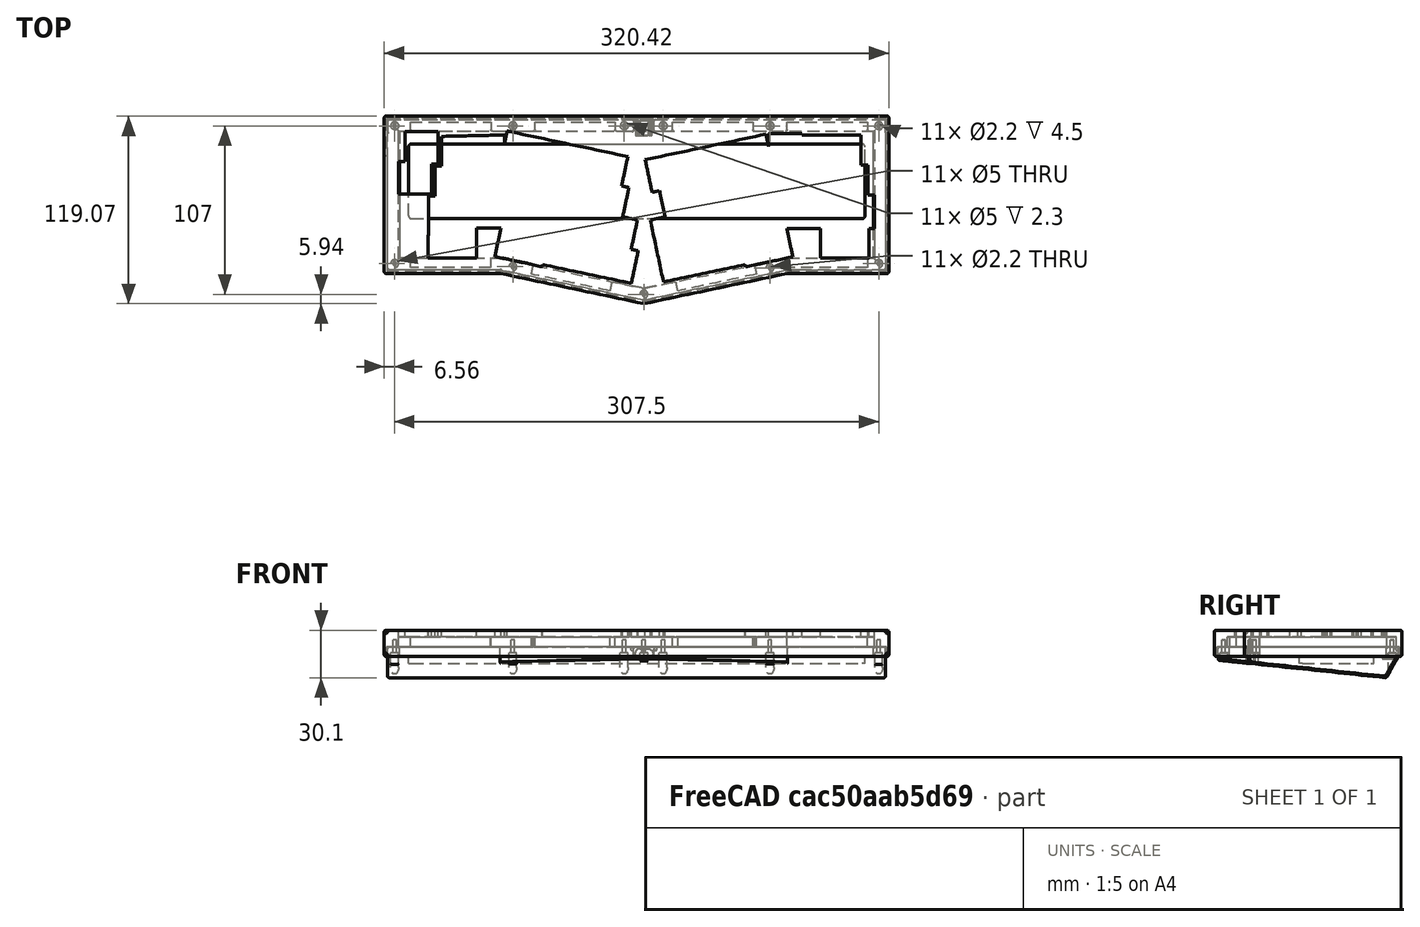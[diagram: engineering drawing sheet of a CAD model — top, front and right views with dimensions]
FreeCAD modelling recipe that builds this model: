
FCSTD DOCUMENT  (FreeCAD 0.19R24291 (Git))
Label: vision-case
License: All rights reserved
LicenseURL: http://en.wikipedia.org/wiki/All_rights_reserved
objects: Part::Cylinder×48, Part::Feature×12, Part::MultiFuse×10, Part::Extrusion×7, Part::Cut×7, Part::Fillet×7, Part::Box×2, Part::FeaturePython×2, Part::Common×1, Part::MultiCommon×1
note: 97 computed .brp shape members not serialized (recipe doc carries the construction recipe); baked Part::Feature solids carry a one-line shape summary decoded from their .brp

FEATURE [Part::Feature] path1505_004
  Placement = pos=(0,-0.8,-22.5) rot=(-1,0,0;0.10472rad)
  shape: bbox 316.2 x 114.2 x 12.01 mm, 0 faces, 0 solids (baked)
FEATURE [Part::Extrusion] Extrude
  Base = -> path1505_004
  Dir = (0,0,1)
  DirMode = 0
  FaceMakerClass = Part::FaceMakerBullseye
  LengthFwd = 100
  LengthRev = 0
  Solid = true
  Symmetric = false
FEATURE [Part::Feature] path1505_3
  shape: bbox 316.2 x 114.9 x 2e-07 mm, 0 faces, 0 solids (baked)
FEATURE [Part::Extrusion] Extrude001
  Base = -> path1505_3
  Dir = (0,0,-1)
  DirMode = 0
  FaceMakerClass = Part::FaceMakerBullseye
  LengthFwd = 100
  LengthRev = 0
  Solid = true
  Symmetric = false
FEATURE [Part::Common] Common
  Base = -> Extrude
  Tool = -> Extrude001
FEATURE [Part::Box] Box  label="立方体"
  AttacherType = Attacher::AttachEngine3D
  Height = 30
  Length = 400
  Placement = pos=(0,-88.5,-20) rot=(-1,0,0;0.523599rad)
  Width = 30
FEATURE [Part::Cut] Cut
  Base = -> Common
  Tool = -> Box
FEATURE [Part::Fillet] Fillet001  label="bottom-base"
  Base = -> Cut
  Edges = 15 edges r=1: [Edge1,Edge2,Edge4,Edge5,Edge6,Edge7,Edge8,Edge9,Edge10,Edge11,Edge18,Edge19,Edge20,Edge21,Edge22]
FEATURE [Part::Feature] path1529_1
  shape: bbox 320.4 x 119.1 x 2e-07 mm, 0 faces, 0 solids (baked)
FEATURE [Part::Feature] path1529_1001
  shape: bbox 317.2 x 115.9 x 2e-07 mm, 0 faces, 0 solids (baked)
FEATURE [Part::MultiFuse] Fusion
  Shapes = -> [path1529_1001,path1529_1]
FEATURE [Part::Feature] path1795_9
  shape: bbox 302.2 x 107.3 x 2e-07 mm, 0 faces, 0 solids (baked)
FEATURE [Part::Feature] path1795_9001
  shape: bbox 320.4 x 119.1 x 2e-07 mm, 0 faces, 0 solids (baked)
FEATURE [Part::MultiFuse] Fusion001
  Placement = pos=(0,0,5.8) rot=(0,0,1;0rad)
  Shapes = -> [path1795_9001,path1795_9]
FEATURE [Part::Extrusion] Extrude003  label="under-middle-base"
  Base = -> Fusion
  Dir = (0,0,1)
  DirMode = 0
  FaceMakerClass = Part::FaceMakerBullseye
  LengthFwd = 5.8
  LengthRev = 0
  Solid = true
  Symmetric = false
FEATURE [Part::Extrusion] Extrude004  label="middle-base"
  Base = -> Fusion001
  Dir = (0,0,1)
  DirMode = 0
  FaceMakerClass = Part::FaceMakerBullseye
  LengthFwd = 6.6
  LengthRev = 0
  Solid = true
  Symmetric = false
FEATURE [Part::Fillet] Fillet002  label="under-middle-base001"
  Base = -> Extrude003
  Edges = 14 edges r=1: [Edge1,Edge2,Edge3,Edge5,Edge6,Edge8,Edge9,Edge11,Edge12,Edge14,Edge15,Edge17,Edge18,Edge20]
FEATURE [Part::Fillet] Fillet003  label="middle-base001"
  Base = -> Extrude004
  Edges = 25 edges r=1: [Edge1,Edge2,Edge5,Edge8,Edge11,Edge14,Edge17,Edge22,Edge23,Edge32,Edge35,Edge44,Edge53,Edge62,Edge68,Edge77,Edge83,Edge92,Edge98,Edge107,Edge116,Edge125,Edge128,Edge131,Edge140]
FEATURE [Part::Cylinder] Cylinder  label="円柱"
  Angle = 360
  AttacherType = Attacher::AttachEngine3D
  Height = 30
  Placement = pos=(51.7,-81,-27.7) rot=(0,0,1;0rad)
  Radius = 2.5
FEATURE [Part::Cylinder] Cylinder001  label="円柱001"
  Angle = 360
  AttacherType = Attacher::AttachEngine3D
  Height = 30
  Placement = pos=(359.2,-81,-27.7) rot=(0,0,1;0rad)
  Radius = 2.5
FEATURE [Part::Cylinder] Cylinder002  label="円柱002"
  Angle = 360
  AttacherType = Attacher::AttachEngine3D
  Height = 30
  Placement = pos=(126.8,-81,-27.7) rot=(0,0,1;0rad)
  Radius = 2.5
FEATURE [Part::Cylinder] Cylinder003  label="円柱003"
  Angle = 360
  AttacherType = Attacher::AttachEngine3D
  Height = 30
  Placement = pos=(197.5,-81,-27.7) rot=(0,0,1;0rad)
  Radius = 2.5
FEATURE [Part::Cylinder] Cylinder004  label="円柱004"
  Angle = 360
  AttacherType = Attacher::AttachEngine3D
  Height = 30
  Placement = pos=(290.1,-81,-27.7) rot=(0,0,1;0rad)
  Radius = 2.5
FEATURE [Part::Cylinder] Cylinder005  label="円柱005"
  Angle = 360
  AttacherType = Attacher::AttachEngine3D
  Height = 30
  Placement = pos=(222.2,-81,-27.7) rot=(0,0,1;0rad)
  Radius = 2.5
FEATURE [Part::Cylinder] Cylinder006  label="円柱006"
  Angle = 360
  AttacherType = Attacher::AttachEngine3D
  Height = 30
  Placement = pos=(51.7,-168.5,-27.7) rot=(0,0,1;0rad)
  Radius = 2.5
FEATURE [Part::Cylinder] Cylinder007  label="円柱007"
  Angle = 360
  AttacherType = Attacher::AttachEngine3D
  Height = 30
  Placement = pos=(359.2,-168.5,-27.7) rot=(0,0,1;0rad)
  Radius = 2.5
FEATURE [Part::Cylinder] Cylinder008  label="円柱008"
  Angle = 360
  AttacherType = Attacher::AttachEngine3D
  Height = 30
  Placement = pos=(126.8,-170.5,-27.7) rot=(0,0,1;0rad)
  Radius = 2.5
FEATURE [Part::Cylinder] Cylinder009  label="円柱009"
  Angle = 360
  AttacherType = Attacher::AttachEngine3D
  Height = 30
  Placement = pos=(290.1,-171.2,-27.7) rot=(0,0,1;0rad)
  Radius = 2.5
FEATURE [Part::Cylinder] Cylinder010  label="円柱010"
  Angle = 360
  AttacherType = Attacher::AttachEngine3D
  Height = 30
  Placement = pos=(210,-188,-27.7) rot=(0,0,1;0rad)
  Radius = 2.5
FEATURE [Part::MultiFuse] Fusion003
  Shapes = -> [Cylinder010,Cylinder009,Cylinder008,Cylinder007,Cylinder006,Cylinder005,Cylinder004,Cylinder003,Cylinder002,Cylinder001,Cylinder]
FEATURE [Part::Cylinder] Cylinder011  label="円柱011"
  Angle = 360
  AttacherType = Attacher::AttachEngine3D
  Height = 38
  Placement = pos=(126.8,-170.5,-27.7) rot=(0,0,1;0rad)
  Radius = 1.1
FEATURE [Part::Cylinder] Cylinder012  label="円柱012"
  Angle = 360
  AttacherType = Attacher::AttachEngine3D
  Height = 38
  Placement = pos=(290.1,-171.2,-27.7) rot=(0,0,1;0rad)
  Radius = 1.1
FEATURE [Part::Cylinder] Cylinder013  label="円柱013"
  Angle = 360
  AttacherType = Attacher::AttachEngine3D
  Height = 38
  Placement = pos=(126.8,-81,-27.7) rot=(0,0,1;0rad)
  Radius = 1.1
FEATURE [Part::Cylinder] Cylinder014  label="円柱014"
  Angle = 360
  AttacherType = Attacher::AttachEngine3D
  Height = 38
  Placement = pos=(210,-188,-27.7) rot=(0,0,1;0rad)
  Radius = 1.1
FEATURE [Part::Cylinder] Cylinder015  label="円柱015"
  Angle = 360
  AttacherType = Attacher::AttachEngine3D
  Height = 38
  Placement = pos=(359.2,-81,-27.7) rot=(0,0,1;0rad)
  Radius = 1.1
FEATURE [Part::Cylinder] Cylinder016  label="円柱016"
  Angle = 360
  AttacherType = Attacher::AttachEngine3D
  Height = 38
  Placement = pos=(197.5,-81,-27.7) rot=(0,0,1;0rad)
  Radius = 1.1
FEATURE [Part::Cylinder] Cylinder017  label="円柱017"
  Angle = 360
  AttacherType = Attacher::AttachEngine3D
  Height = 38
  Placement = pos=(290.1,-81,-27.7) rot=(0,0,1;0rad)
  Radius = 1.1
FEATURE [Part::Cylinder] Cylinder018  label="円柱018"
  Angle = 360
  AttacherType = Attacher::AttachEngine3D
  Height = 38
  Placement = pos=(51.7,-81,-27.7) rot=(0,0,1;0rad)
  Radius = 1.1
FEATURE [Part::Cylinder] Cylinder019  label="円柱019"
  Angle = 360
  AttacherType = Attacher::AttachEngine3D
  Height = 38
  Placement = pos=(222.2,-81,-27.7) rot=(0,0,1;0rad)
  Radius = 1.1
FEATURE [Part::Cylinder] Cylinder020  label="円柱020"
  Angle = 360
  AttacherType = Attacher::AttachEngine3D
  Height = 38
  Placement = pos=(359.2,-168.5,-27.7) rot=(0,0,1;0rad)
  Radius = 1.1
FEATURE [Part::Cylinder] Cylinder021  label="円柱021"
  Angle = 360
  AttacherType = Attacher::AttachEngine3D
  Height = 38
  Placement = pos=(51.7,-168.5,-27.7) rot=(0,0,1;0rad)
  Radius = 1.1
FEATURE [Part::MultiFuse] Fusion004
  Shapes = -> [Cylinder014,Cylinder012,Cylinder011,Cylinder020,Cylinder021,Cylinder019,Cylinder017,Cylinder016,Cylinder013,Cylinder015,Cylinder018]
FEATURE [Part::Cylinder] Cylinder022  label="円柱022"
  Angle = 360
  AttacherType = Attacher::AttachEngine3D
  Height = 30
  Placement = pos=(126.8,-170.5,-27.7) rot=(0,0,1;0rad)
  Radius = 2.5
FEATURE [Part::Cylinder] Cylinder023  label="円柱023"
  Angle = 360
  AttacherType = Attacher::AttachEngine3D
  Height = 30
  Placement = pos=(290.1,-171.2,-27.7) rot=(0,0,1;0rad)
  Radius = 2.5
FEATURE [Part::Cylinder] Cylinder024  label="円柱024"
  Angle = 360
  AttacherType = Attacher::AttachEngine3D
  Height = 30
  Placement = pos=(126.8,-81,-27.7) rot=(0,0,1;0rad)
  Radius = 2.5
FEATURE [Part::Cylinder] Cylinder025  label="円柱025"
  Angle = 360
  AttacherType = Attacher::AttachEngine3D
  Height = 30
  Placement = pos=(210,-188,-27.7) rot=(0,0,1;0rad)
  Radius = 2.5
FEATURE [Part::Cylinder] Cylinder026  label="円柱026"
  Angle = 360
  AttacherType = Attacher::AttachEngine3D
  Height = 30
  Placement = pos=(359.2,-81,-27.7) rot=(0,0,1;0rad)
  Radius = 2.5
FEATURE [Part::Cylinder] Cylinder027  label="円柱027"
  Angle = 360
  AttacherType = Attacher::AttachEngine3D
  Height = 30
  Placement = pos=(197.5,-81,-27.7) rot=(0,0,1;0rad)
  Radius = 2.5
FEATURE [Part::Cylinder] Cylinder028  label="円柱028"
  Angle = 360
  AttacherType = Attacher::AttachEngine3D
  Height = 30
  Placement = pos=(290.1,-81,-27.7) rot=(0,0,1;0rad)
  Radius = 2.5
FEATURE [Part::Cylinder] Cylinder029  label="円柱029"
  Angle = 360
  AttacherType = Attacher::AttachEngine3D
  Height = 30
  Placement = pos=(51.7,-81,-27.7) rot=(0,0,1;0rad)
  Radius = 2.5
FEATURE [Part::Cylinder] Cylinder030  label="円柱030"
  Angle = 360
  AttacherType = Attacher::AttachEngine3D
  Height = 30
  Placement = pos=(222.2,-81,-27.7) rot=(0,0,1;0rad)
  Radius = 2.5
FEATURE [Part::Cylinder] Cylinder031  label="円柱031"
  Angle = 360
  AttacherType = Attacher::AttachEngine3D
  Height = 30
  Placement = pos=(359.2,-168.5,-27.7) rot=(0,0,1;0rad)
  Radius = 2.5
FEATURE [Part::Cylinder] Cylinder032  label="円柱032"
  Angle = 360
  AttacherType = Attacher::AttachEngine3D
  Height = 30
  Placement = pos=(51.7,-168.5,-27.7) rot=(0,0,1;0rad)
  Radius = 2.5
FEATURE [Part::MultiFuse] Fusion005
  Shapes = -> [Cylinder025,Cylinder023,Cylinder022,Cylinder031,Cylinder032,Cylinder030,Cylinder028,Cylinder027,Cylinder024,Cylinder026,Cylinder029]
FEATURE [Part::Cylinder] Cylinder033  label="円柱033"
  Angle = 360
  AttacherType = Attacher::AttachEngine3D
  Height = 38
  Placement = pos=(126.8,-81,-27.7) rot=(0,0,1;0rad)
  Radius = 1.1
FEATURE [Part::Cylinder] Cylinder034  label="円柱034"
  Angle = 360
  AttacherType = Attacher::AttachEngine3D
  Height = 38
  Placement = pos=(51.7,-81,-27.7) rot=(0,0,1;0rad)
  Radius = 1.1
FEATURE [Part::Cylinder] Cylinder035  label="円柱035"
  Angle = 360
  AttacherType = Attacher::AttachEngine3D
  Height = 38
  Placement = pos=(197.5,-81,-27.7) rot=(0,0,1;0rad)
  Radius = 1.1
FEATURE [Part::Cylinder] Cylinder036  label="円柱036"
  Angle = 360
  AttacherType = Attacher::AttachEngine3D
  Height = 38
  Placement = pos=(222.2,-81,-27.7) rot=(0,0,1;0rad)
  Radius = 1.1
FEATURE [Part::Cylinder] Cylinder037  label="円柱037"
  Angle = 360
  AttacherType = Attacher::AttachEngine3D
  Height = 38
  Placement = pos=(359.2,-168.5,-27.7) rot=(0,0,1;0rad)
  Radius = 1.1
FEATURE [Part::Cylinder] Cylinder038  label="円柱038"
  Angle = 360
  AttacherType = Attacher::AttachEngine3D
  Height = 38
  Placement = pos=(359.2,-81,-27.7) rot=(0,0,1;0rad)
  Radius = 1.1
FEATURE [Part::Cylinder] Cylinder039  label="円柱039"
  Angle = 360
  AttacherType = Attacher::AttachEngine3D
  Height = 38
  Placement = pos=(126.8,-170.5,-27.7) rot=(0,0,1;0rad)
  Radius = 1.1
FEATURE [Part::Cylinder] Cylinder040  label="円柱040"
  Angle = 360
  AttacherType = Attacher::AttachEngine3D
  Height = 38
  Placement = pos=(290.1,-171.2,-27.7) rot=(0,0,1;0rad)
  Radius = 1.1
FEATURE [Part::Cylinder] Cylinder041  label="円柱041"
  Angle = 360
  AttacherType = Attacher::AttachEngine3D
  Height = 38
  Placement = pos=(210,-188,-27.7) rot=(0,0,1;0rad)
  Radius = 1.1
FEATURE [Part::Cylinder] Cylinder042  label="円柱042"
  Angle = 360
  AttacherType = Attacher::AttachEngine3D
  Height = 38
  Placement = pos=(290.1,-81,-27.7) rot=(0,0,1;0rad)
  Radius = 1.1
FEATURE [Part::Cylinder] Cylinder043  label="円柱043"
  Angle = 360
  AttacherType = Attacher::AttachEngine3D
  Height = 38
  Placement = pos=(51.7,-168.5,-27.7) rot=(0,0,1;0rad)
  Radius = 1.1
FEATURE [Part::MultiFuse] Fusion006
  Shapes = -> [Cylinder041,Cylinder040,Cylinder039,Cylinder037,Cylinder043,Cylinder036,Cylinder042,Cylinder035,Cylinder033,Cylinder038,Cylinder034]
FEATURE [Part::Cut] Cut002  label="bottom-base001"
  Base = -> Fillet001
  Tool = -> Fusion003
FEATURE [Part::Cut] Cut005  label="middle"
  Base = -> Fillet003
  Tool = -> Fusion006
FEATURE [Part::Box] Box001  label="立方体001"
  AttacherType = Attacher::AttachEngine3D
  Height = 4.5
  Length = 290
  Placement = pos=(60.5,-140,-4.5) rot=(0,0,1;0rad)
  Width = 47.5
FEATURE [Part::Fillet] Fillet005
  Base = -> Box001
  Edges = 4 edges r=2: [Edge1,Edge3,Edge5,Edge7]
FEATURE [Part::Cut] Cut006  label="bottom-base002"
  Base = -> Cut002
  Tool = -> Fillet005
FEATURE [Part::Cylinder] cylinder
  Angle = 360
  AttacherType = Attacher::AttachEngine3D
  Height = 10
  Radius = 3.21
FEATURE [Part::Cylinder] cylinder010
  Angle = 360
  AttacherType = Attacher::AttachEngine3D
  Height = 10
  Placement = pos=(4.88,0,0) rot=(0,0,1;0rad)
  Radius = 3.21
FEATURE [Part::FeaturePython] hull  # WARN: FeaturePython — macro-defined, semantics opaque (R4)
  Arguments = []
  Children = -> [cylinder,cylinder010]
  Operation = hull
  Placement = pos=(207.6,-70,1.62) rot=(1,0,0;1.5708rad)
FEATURE [Part::Cylinder] cylinder011
  Angle = 360
  AttacherType = Attacher::AttachEngine3D
  Height = 10
  Placement = pos=(4.88,0,0) rot=(0,0,1;0rad)
  Radius = 3.21
FEATURE [Part::Cylinder] cylinder012
  Angle = 360
  AttacherType = Attacher::AttachEngine3D
  Height = 10
  Radius = 3.21
FEATURE [Part::FeaturePython] hull001  # WARN: FeaturePython — macro-defined, semantics opaque (R4)
  Arguments = []
  Children = -> [cylinder012,cylinder011]
  Operation = hull
  Placement = pos=(207.6,-77.3,1.62) rot=(1,0,0;1.5708rad)
FEATURE [Part::Cut] Cut007  label="under-middle"
  Base = -> Fillet002
  Tool = -> hull
FEATURE [Part::Cut] Cut008  label="bottom"
  Base = -> Cut006
  Tool = -> hull001
FEATURE [Part::Feature] path2008_2
  shape: bbox 25.26 x 39.55 x 2e-07 mm, 0 faces, 0 solids (baked)
FEATURE [Part::Feature] path2008_2001
  shape: bbox 133.4 x 96.75 x 2e-07 mm, 0 faces, 0 solids (baked)
FEATURE [Part::Feature] path2008_2002
  shape: bbox 145.6 x 94.34 x 2e-07 mm, 0 faces, 0 solids (baked)
FEATURE [Part::Feature] path2008_2003
  shape: bbox 320.4 x 119.1 x 2e-07 mm, 0 faces, 0 solids (baked)
FEATURE [Part::MultiFuse] Fusion012
  Placement = pos=(0,0,12.4) rot=(0,0,1;0rad)
  Shapes = -> [path2008_2002,path2008_2003,path2008_2001,path2008_2]
FEATURE [Part::Extrusion] Extrude005
  Base = -> Fusion012
  Dir = (0,0,1)
  DirMode = 0
  FaceMakerClass = Part::FaceMakerBullseye
  LengthFwd = 4.1
  LengthRev = 0
  Solid = true
  Symmetric = false
FEATURE [Part::Fillet] Fillet006  label="top"
  Base = -> Extrude005
  Edges = 14 edges r=1: [Edge1,Edge2,Edge4,Edge5,Edge7,Edge8,Edge10,Edge11,Edge13,Edge14,Edge16,Edge17,Edge19,Edge21]
FEATURE [Part::MultiFuse] Fusion013  label="top-case"
  Shapes = -> [Fillet006,Cut007,Cut005]
FEATURE [Part::Feature] path1497_6_3_5
  shape: bbox 316.2 x 114.9 x 2e-07 mm, 0 faces, 0 solids (baked)
FEATURE [Part::Extrusion] Extrude006
  Base = -> path1497_6_3_5
  Dir = (0,0,1)
  DirMode = 0
  FaceMakerClass = Part::FaceMakerBullseye
  LengthFwd = 5.8
  LengthRev = 0
  Solid = true
  Symmetric = false
FEATURE [Part::Fillet] Fillet
  Base = -> Extrude006
  Edges = 29 edges r=1: [Edge1,Edge2,Edge4,Edge7,Edge10,Edge13,Edge16,Edge19,Edge22,Edge25,Edge26,Edge28,Edge29,Edge31,Edge32,Edge34,Edge35,Edge37,Edge38,Edge40,Edge41,Edge43,Edge44,Edge46,Edge47,Edge49,Edge50,Edge52,Edge54]
FEATURE [Part::MultiFuse] Fusion014
  Shapes = -> [Fusion004,Fusion005]
FEATURE [Part::Feature] path1497_6_3_006
  shape: bbox 316.2 x 114.9 x 2e-07 mm, 0 faces, 0 solids (baked)
FEATURE [Part::Extrusion] Extrude007
  Base = -> path1497_6_3_006
  Dir = (0,0,1)
  DirMode = 0
  FaceMakerClass = Part::FaceMakerBullseye
  LengthFwd = 5.8
  LengthRev = 0
  Solid = true
  Symmetric = false
FEATURE [Part::Fillet] Fillet007
  Base = -> Extrude007
  Edges = 29 edges r=1: [Edge1,Edge2,Edge4,Edge7,Edge10,Edge13,Edge16,Edge19,Edge22,Edge25,Edge26,Edge28,Edge29,Edge31,Edge32,Edge34,Edge35,Edge37,Edge38,Edge40,Edge41,Edge43,Edge44,Edge46,Edge47,Edge49,Edge50,Edge52,Edge54]
FEATURE [Part::MultiCommon] Common001
  Shapes = -> [Fusion014,Fillet007]
FEATURE [Part::Cut] Cut009  label="bottom-middle"
  Base = -> Fillet
  Tool = -> Common001
FEATURE [Part::MultiFuse] Fusion015  label="bottom-case"
  Shapes = -> [Cut008,Cut009]
